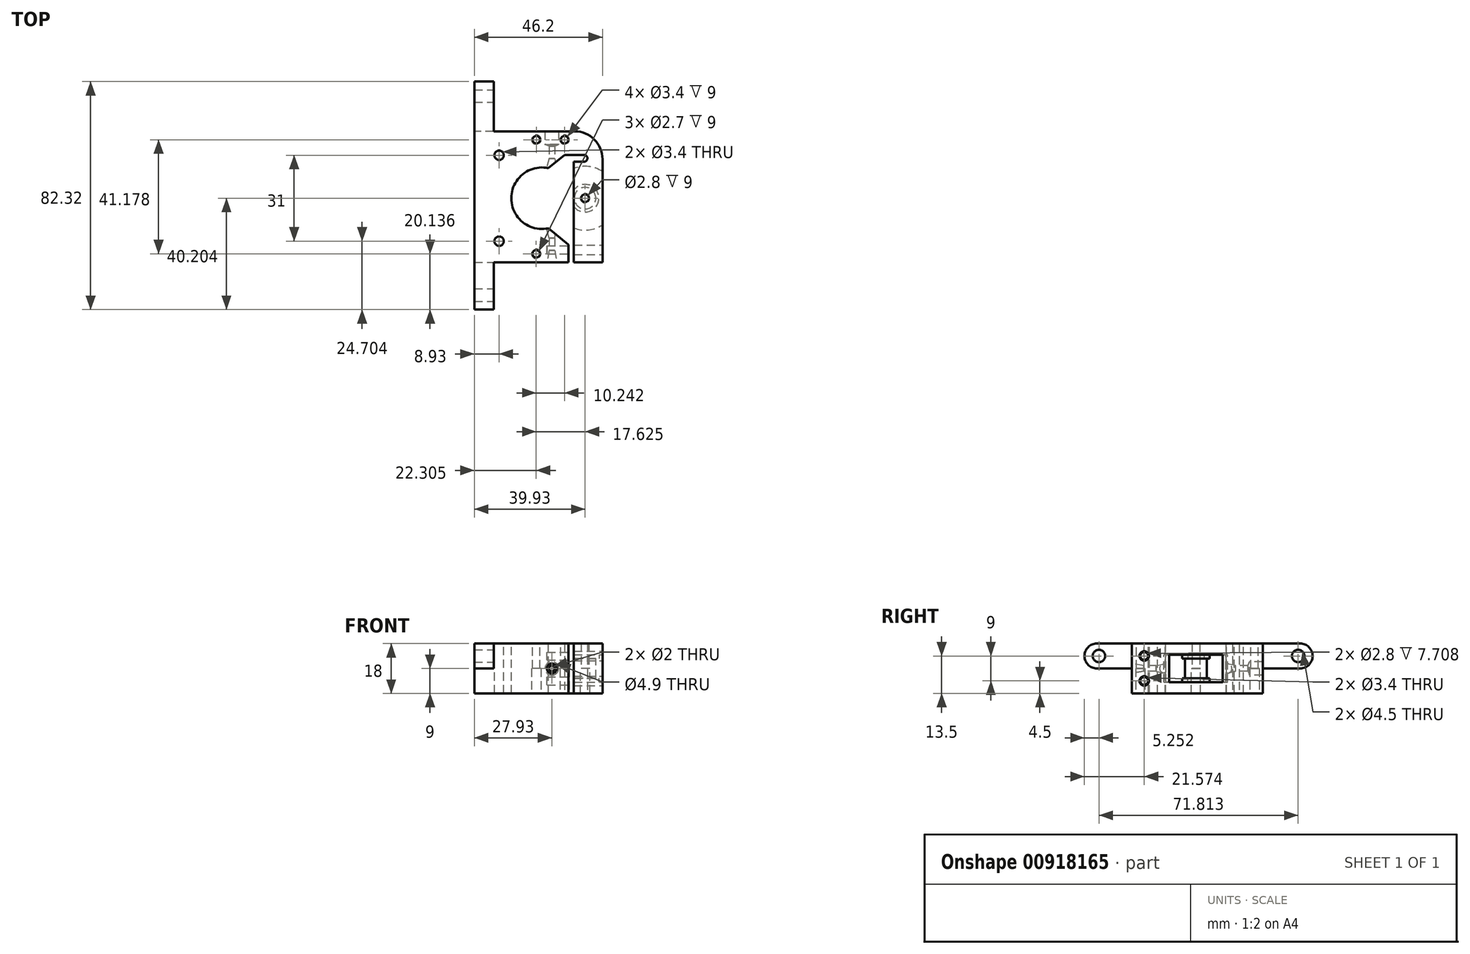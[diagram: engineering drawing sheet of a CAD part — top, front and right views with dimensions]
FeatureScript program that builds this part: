
annotation { "Feature Type Name" : "Feature", "Feature Type Description" : "" }
export const myFeature = defineFeature(function(context is Context, id is Id, definition is map)
    precondition{}
    {
        {
            var Q0;
            Q0=qCreatedBy(makeId("Top.planeOp"),FACE);
            var sketch = newSketch(context, id + "F0", { "sketchPlane" : qUnion([Q0])});
            skLineSegment(sketch, "E0", {"start": v(-24.43, 29.94) * mm, "end": v(-24.43, -17.36) * mm});
            skLineSegment(sketch, "E1", {"start": v(-24.43, -17.36) * mm, "end": v(-24.43, -17.36) * mm});
            skLineSegment(sketch, "E2", {"start": v(-24.43, -17.36) * mm, "end": v(-24.43, -17.35) * mm});
            skLineSegment(sketch, "E3", {"start": v(-24.43, -17.35) * mm, "end": v(9.48, -17.35) * mm});
            skLineSegment(sketch, "E4", {"start": v(9.48, -17.35) * mm, "end": v(9.48, 21.46) * mm});
            skLineSegment(sketch, "E5", {"start": v(9.48, 21.46) * mm, "end": v(15.14, 21.46) * mm});
            skLineSegment(sketch, "E6", {"start": v(15.14, 19) * mm, "end": v(11.48, 19) * mm});
            skLineSegment(sketch, "E7", {"start": v(11.48, 19) * mm, "end": v(11.48, -17.35) * mm});
            skLineSegment(sketch, "E8", {"start": v(11.48, -17.35) * mm, "end": v(21.77, -17.35) * mm});
            skLineSegment(sketch, "E9", {"start": v(21.77, -17.35) * mm, "end": v(21.77, 29.94) * mm});
            skLineSegment(sketch, "E10", {"start": v(21.77, 29.94) * mm, "end": v(-24.43, 29.94) * mm});
            skCircle(sketch, "E11", {"center": v(-2.07, 26.93) * mm, "radius": 1.35 * mm});
            skCircle(sketch, "E12", {"center": v(8.12, 26.93) * mm, "radius": 1.35 * mm});
            skCircle(sketch, "E13", {"center": v(-2.12, -14.24) * mm, "radius": 1.35 * mm});
            skArc(sketch, "E14", {"start": v(15.14, 19) * mm, "mid": v(16.36, 20.23) * mm, "end": v(15.14, 21.46) * mm});
            skCircle(sketch, "E15", {"center": v(-2.07, 26.93) * mm, "radius": 1.7 * mm});
            skCircle(sketch, "E16", {"center": v(8.12, 26.93) * mm, "radius": 1.7 * mm});
            skCircle(sketch, "E17", {"center": v(-2.12, -14.24) * mm, "radius": 1.7 * mm});
            skSolve(sketch);
        }
        {
            var Q0;
            Q0=makeQuery(id+"F0.imprint","IMPRINT",FACE,{"disambiguationData":[TD([[makeQuery(id+"F0.imprint","IMPRINT",EDGE,{"derivedFrom":sQuery(id+"F0.wireOp",EDGE,"E0")}),1.0]])]});
            extrude(context, id + "F1", {"entities" : qUnion([Q0]), "depth" : 9 * mm});
        }
        {
            var Q0;
            Q0=makeQuery(id+"F1.opExtrude","CAP_FACE",FACE,{"disambiguationData":[OSD([sQuery(id+"F0.wireOp",EDGE,"E0"),sQuery(id+"F0.wireOp",EDGE,"E1"),sQuery(id+"F0.wireOp",EDGE,"E2"),sQuery(id+"F0.wireOp",EDGE,"E3"),sQuery(id+"F0.wireOp",EDGE,"E4"),sQuery(id+"F0.wireOp",EDGE,"E5"),sQuery(id+"F0.wireOp",EDGE,"E6"),sQuery(id+"F0.wireOp",EDGE,"E7"),sQuery(id+"F0.wireOp",EDGE,"E8"),sQuery(id+"F0.wireOp",EDGE,"E9"),sQuery(id+"F0.wireOp",EDGE,"E10"),sQuery(id+"F0.wireOp",EDGE,"604cad85-587a-4b7d-8070-06f4cba85480"),sQuery(id+"F0.wireOp",EDGE,"6e5e38c1-5bff-4efe-a8c5-b84022f0a049"),sQuery(id+"F0.wireOp",EDGE,"b8144507-9dd7-4af4-87a3-7b649dd00ae6"),sQuery(id+"F0.wireOp",EDGE,"b9c2cb7c-5e58-4995-888e-a78f0403fbb5"),sQuery(id+"F0.wireOp",EDGE,"885990ab-7576-4c23-8475-595d2769e284"),sQuery(id+"F0.wireOp",EDGE,"E11"),sQuery(id+"F0.wireOp",EDGE,"E12"),sQuery(id+"F0.wireOp",EDGE,"E13"),sQuery(id+"F0.wireOp",EDGE,"E14")])],"isStart":false});
            var sketch = newSketch(context, id + "F2", { "sketchPlane" : qUnion([Q0])});
            skCircle(sketch, "E18", {"center": v(0, 5.82) * mm, "radius": 11.1 * mm});
            skCircle(sketch, "E19", {"center": v(-15.5, 21.32) * mm, "radius": 1.7 * mm});
            skCircle(sketch, "E20", {"center": v(-15.5, -9.68) * mm, "radius": 1.7 * mm});
            skSolve(sketch);
        }
        {
            var Q0;
            Q0=qSketchRegion(id+"F2",true);
            extrude(context, id + "F3", {"entities" : qUnion([Q0]), "operationType" : NewBodyOperationType.REMOVE, "endBound" : BoundingType.THROUGH_ALL, "oppositeDirection" : true, "depth" : 25 * mm});
        }
        {
            var Q0;
            Q0=makeQuery(id+"F1.opExtrude","CAP_FACE",FACE,{"disambiguationData":[OSD([sQuery(id+"F0.wireOp",EDGE,"E0"),sQuery(id+"F0.wireOp",EDGE,"E1"),sQuery(id+"F0.wireOp",EDGE,"E2"),sQuery(id+"F0.wireOp",EDGE,"E3"),sQuery(id+"F0.wireOp",EDGE,"E4"),sQuery(id+"F0.wireOp",EDGE,"E5"),sQuery(id+"F0.wireOp",EDGE,"E6"),sQuery(id+"F0.wireOp",EDGE,"E7"),sQuery(id+"F0.wireOp",EDGE,"E8"),sQuery(id+"F0.wireOp",EDGE,"E9"),sQuery(id+"F0.wireOp",EDGE,"E10"),sQuery(id+"F0.wireOp",EDGE,"604cad85-587a-4b7d-8070-06f4cba85480"),sQuery(id+"F0.wireOp",EDGE,"6e5e38c1-5bff-4efe-a8c5-b84022f0a049"),sQuery(id+"F0.wireOp",EDGE,"E11"),sQuery(id+"F0.wireOp",EDGE,"E12"),sQuery(id+"F0.wireOp",EDGE,"E13"),sQuery(id+"F0.wireOp",EDGE,"E14")])],"isStart":false});
            var sketch = newSketch(context, id + "F4", { "sketchPlane" : qUnion([Q0])});
            skCircle(sketch, "E21", {"center": v(15.5, 5.82) * mm, "radius": 11.5 * mm});
            skCircle(sketch, "E22", {"center": v(15.5, 5.82) * mm, "radius": 5 * mm});
            skCircle(sketch, "E23", {"center": v(15.5, 5.82) * mm, "radius": 3.9 * mm});
            skLineSegment(sketch, "E24", {"start": v(0, 5.82) * mm, "end": v(31, 5.82) * mm, "construction": true});
            skCircle(sketch, "E25", {"center": v(15.5, 5.82) * mm, "radius": 1.4 * mm});
            skCircle(sketch, "E26", {"center": v(15.5, 5.82) * mm, "radius": 1.7 * mm});
            skSolve(sketch);
        }
        {
            var Q0;
            Q0=makeQuery(id+"F4.imprint","IMPRINT",FACE,{"disambiguationData":[TD([[makeQuery(id+"F4.imprint","IMPRINT",EDGE,{"derivedFrom":sQuery(id+"F4.wireOp",EDGE,"E22")}),-1.0]])]});
            extrude(context, id + "F5", {"entities" : qUnion([Q0]), "operationType" : NewBodyOperationType.REMOVE, "oppositeDirection" : true, "depth" : 5 * mm});
        }
        {
            var Q0;
            Q0=makeQuery(id+"F4.imprint","IMPRINT",FACE,{"disambiguationData":[TD([[makeQuery(id+"F4.imprint","IMPRINT",EDGE,{"derivedFrom":sQuery(id+"F4.wireOp",EDGE,"E22")}),1.0]])]});
            var Q1;
            Q1=makeQuery(id+"F4.imprint","IMPRINT",FACE,{"disambiguationData":[TD([[makeQuery(id+"F4.imprint","IMPRINT",EDGE,{"derivedFrom":sQuery(id+"F4.wireOp",EDGE,"E23")}),-1.0]])]});
            extrude(context, id + "F6", {"entities" : qUnion([Q0, Q1]), "operationType" : NewBodyOperationType.REMOVE, "oppositeDirection" : true, "depth" : 3.5 * mm});
        }
        {
            var Q0;
            {var subQ0=sQuery(id+"F0.wireOp",EDGE,"E0");var subQ1=sQuery(id+"F0.wireOp",EDGE,"E1");var subQ2=sQuery(id+"F0.wireOp",EDGE,"E2");var subQ3=sQuery(id+"F0.wireOp",EDGE,"E3");var subQ4=sQuery(id+"F0.wireOp",EDGE,"E4");var subQ5=sQuery(id+"F0.wireOp",EDGE,"E5");var subQ6=sQuery(id+"F0.wireOp",EDGE,"E6");var subQ7=sQuery(id+"F0.wireOp",EDGE,"E7");var subQ8=sQuery(id+"F0.wireOp",EDGE,"E9");var subQ9=sQuery(id+"F0.wireOp",EDGE,"E10");var subQ10=sQuery(id+"F0.wireOp",EDGE,"604cad85-587a-4b7d-8070-06f4cba85480");var subQ11=sQuery(id+"F0.wireOp",EDGE,"6e5e38c1-5bff-4efe-a8c5-b84022f0a049");var subQ12=sQuery(id+"F0.wireOp",EDGE,"E11");var subQ13=sQuery(id+"F0.wireOp",EDGE,"E12");var subQ14=sQuery(id+"F0.wireOp",EDGE,"E13");var subQ15=sQuery(id+"F0.wireOp",EDGE,"E14");Q0=makeQuery(id+"F5.boolean.opBoolean","SPLIT",FACE,{"disambiguationData":[TD([makeQuery(id+"F1.opExtrude","SWEPT_FACE",FACE,{"disambiguationData":[OSD([subQ0])]})])],"derivedFrom":makeQuery(id+"F1.opExtrude","CAP_FACE",FACE,{"disambiguationData":[OSD([subQ0,subQ1,subQ2,subQ3,subQ4,subQ5,subQ6,subQ7,sQuery(id+"F0.wireOp",EDGE,"E8"),subQ8,subQ9,subQ10,subQ11,subQ12,subQ13,subQ14,subQ15])],"isStart":false})});}
            var sketch = newSketch(context, id + "F7", { "sketchPlane" : qUnion([Q0])});
            skLineSegment(sketch, "E27", {"start": v(2.5, 24.65) * mm, "end": v(2.5, 20.21) * mm});
            skLineSegment(sketch, "E28", {"start": v(2.5, 20.21) * mm, "end": v(1.31, 15.18) * mm});
            skLineSegment(sketch, "E29", {"start": v(1.31, 15.18) * mm, "end": v(3.5, 15.18) * mm});
            skLineSegment(sketch, "E30", {"start": v(3.5, 15.18) * mm, "end": v(3.5, 30.2) * mm});
            skLineSegment(sketch, "E31", {"start": v(0, 5.82) * mm, "end": v(31.4, 5.82) * mm, "construction": true});
            skLineSegment(sketch, "E32.1.MirrorCS", {"start": v(3.5, -3.53) * mm, "end": v(3.5, -18.54) * mm});
            skLineSegment(sketch, "E32.3.MirrorCS", {"start": v(1.31, -3.53) * mm, "end": v(3.5, -3.53) * mm});
            skLineSegment(sketch, "E32.4.MirrorCS", {"start": v(2.5, -8.56) * mm, "end": v(1.31, -3.53) * mm});
            skLineSegment(sketch, "E32.5.MirrorCS", {"start": v(2.5, -13) * mm, "end": v(2.5, -8.56) * mm});
            skLineSegment(sketch, "E32.6.MirrorCS", {"start": v(3.5, -18.54) * mm, "end": v(1.5, -18.54) * mm});
            skLineSegment(sketch, "E33", {"start": v(3.5, 30.2) * mm, "end": v(1.05, 30.2) * mm});
            skLineSegment(sketch, "E34", {"start": v(1.05, 30.2) * mm, "end": v(1.05, 25.2) * mm});
            skLineSegment(sketch, "E35", {"start": v(2.5, 24.65) * mm, "end": v(1.05, 25.2) * mm});
            skLineSegment(sketch, "E36", {"start": v(2.5, -13) * mm, "end": v(1.5, -18.54) * mm});
            skSolve(sketch);
        }
        {
            var Q0;
            Q0=qSketchRegion(id+"F7",true);
            var Q1;
            Q1=sQuery(id+"F7.wireOp",EDGE,"E30");
            revolve(context, id + "F8", {"entities" : qUnion([Q0]), "axis" : qUnion([Q1]), "revolveType" : RevolveType.FULL});
        }
        {
            var Q0;
            Q0=makeQuery(id+"F8.opRevolve","SWEPT_BODY",BODY,{"disambiguationData":[OSD([sQuery(id+"F7.wireOp",EDGE,"0e4a01cc-4869-4b9d-8ca2-1c94110d196d"),sQuery(id+"F7.wireOp",EDGE,"4d913e13-2244-4a79-84d2-82f6c5de00b3"),sQuery(id+"F7.wireOp",EDGE,"E27"),sQuery(id+"F7.wireOp",EDGE,"E28"),sQuery(id+"F7.wireOp",EDGE,"E29"),sQuery(id+"F7.wireOp",EDGE,"E30"),sQuery(id+"F7.wireOp",EDGE,"0bbee7b9-97e0-41c3-ac0e-625151f8027d")])]});
            var Q1;
            Q1=makeQuery(id+"F1.opExtrude","SWEPT_BODY",BODY,{"disambiguationData":[OSD([sQuery(id+"F0.wireOp",EDGE,"E0"),sQuery(id+"F0.wireOp",EDGE,"E1"),sQuery(id+"F0.wireOp",EDGE,"E2"),sQuery(id+"F0.wireOp",EDGE,"E3"),sQuery(id+"F0.wireOp",EDGE,"E4"),sQuery(id+"F0.wireOp",EDGE,"E5"),sQuery(id+"F0.wireOp",EDGE,"E6"),sQuery(id+"F0.wireOp",EDGE,"E7"),sQuery(id+"F0.wireOp",EDGE,"E8"),sQuery(id+"F0.wireOp",EDGE,"E9"),sQuery(id+"F0.wireOp",EDGE,"E10"),sQuery(id+"F0.wireOp",EDGE,"604cad85-587a-4b7d-8070-06f4cba85480"),sQuery(id+"F0.wireOp",EDGE,"6e5e38c1-5bff-4efe-a8c5-b84022f0a049"),sQuery(id+"F0.wireOp",EDGE,"E11"),sQuery(id+"F0.wireOp",EDGE,"E12"),sQuery(id+"F0.wireOp",EDGE,"E13"),sQuery(id+"F0.wireOp",EDGE,"E14")])]});
            booleanBodies(context, id + "F9", {"operationType" : BooleanOperationType.SUBTRACTION, "tools" : qUnion([Q0]), "targets" : qUnion([Q1]), "keepTools" : true});
        }
        {
            var Q0;
            Q0=makeQuery(id+"F8.opRevolve","SWEPT_BODY",BODY,{"disambiguationData":[OSD([sQuery(id+"F7.wireOp",EDGE,"E32.0.MirrorCS"),sQuery(id+"F7.wireOp",EDGE,"E32.1.MirrorCS"),sQuery(id+"F7.wireOp",EDGE,"E32.2.MirrorCS"),sQuery(id+"F7.wireOp",EDGE,"E32.3.MirrorCS"),sQuery(id+"F7.wireOp",EDGE,"E32.4.MirrorCS"),sQuery(id+"F7.wireOp",EDGE,"E32.5.MirrorCS"),sQuery(id+"F7.wireOp",EDGE,"E32.6.MirrorCS")])]});
            var Q1;
            Q1=makeQuery(id+"F1.opExtrude","SWEPT_BODY",BODY,{"disambiguationData":[OSD([sQuery(id+"F0.wireOp",EDGE,"E0"),sQuery(id+"F0.wireOp",EDGE,"E1"),sQuery(id+"F0.wireOp",EDGE,"E2"),sQuery(id+"F0.wireOp",EDGE,"E3"),sQuery(id+"F0.wireOp",EDGE,"E4"),sQuery(id+"F0.wireOp",EDGE,"E5"),sQuery(id+"F0.wireOp",EDGE,"E6"),sQuery(id+"F0.wireOp",EDGE,"E7"),sQuery(id+"F0.wireOp",EDGE,"E8"),sQuery(id+"F0.wireOp",EDGE,"E9"),sQuery(id+"F0.wireOp",EDGE,"E10"),sQuery(id+"F0.wireOp",EDGE,"604cad85-587a-4b7d-8070-06f4cba85480"),sQuery(id+"F0.wireOp",EDGE,"6e5e38c1-5bff-4efe-a8c5-b84022f0a049"),sQuery(id+"F0.wireOp",EDGE,"E11"),sQuery(id+"F0.wireOp",EDGE,"E12"),sQuery(id+"F0.wireOp",EDGE,"E13"),sQuery(id+"F0.wireOp",EDGE,"E14")])]});
            booleanBodies(context, id + "F10", {"operationType" : BooleanOperationType.SUBTRACTION, "tools" : qUnion([Q0]), "targets" : qUnion([Q1]), "keepTools" : true});
        }
        {
            var Q0;
            Q0=makeQuery(id+"F1.opExtrude","SWEPT_EDGE",EDGE,{"disambiguationData":[OSD([sQuery(id+"F0.wireOp",EDGE,"E9"),sQuery(id+"F0.wireOp",EDGE,"E10")])]});
            fillet(context, id + "F11", {"entities" : qUnion([Q0]), "radius" : 10 * mm, "tangentPropagation" : true, "allowEdgeOverflow" : false});
        }
        {
            var Q0;
            Q0=qSketchRegion(id+"F0",true);
            var Q1;
            Q1=makeQuery(id+"F0.imprint","IMPRINT",FACE,{"disambiguationData":[TD([[makeQuery(id+"F0.imprint","IMPRINT",EDGE,{"derivedFrom":sQuery(id+"F0.wireOp",EDGE,"E12")}),-1.0]])]});
            var Q2;
            Q2=makeQuery(id+"F0.imprint","IMPRINT",FACE,{"disambiguationData":[TD([[makeQuery(id+"F0.imprint","IMPRINT",EDGE,{"derivedFrom":sQuery(id+"F0.wireOp",EDGE,"E11")}),-1.0]])]});
            var Q3;
            Q3=makeQuery(id+"F0.imprint","IMPRINT",FACE,{"disambiguationData":[TD([[makeQuery(id+"F0.imprint","IMPRINT",EDGE,{"derivedFrom":sQuery(id+"F0.wireOp",EDGE,"E13")}),-1.0]])]});
            extrude(context, id + "F12", {"entities" : qUnion([Q0, Q1, Q2, Q3]), "oppositeDirection" : true, "depth" : 9 * mm});
        }
        {
            var Q0;
            Q0=makeQuery(id+"F12.opExtrude","SWEPT_BODY",BODY,{"disambiguationData":[OSD([sQuery(id+"F0.wireOp",EDGE,"E0"),sQuery(id+"F0.wireOp",EDGE,"E3"),sQuery(id+"F0.wireOp",EDGE,"E4"),sQuery(id+"F0.wireOp",EDGE,"E5"),sQuery(id+"F0.wireOp",EDGE,"E6"),sQuery(id+"F0.wireOp",EDGE,"E7"),sQuery(id+"F0.wireOp",EDGE,"E8"),sQuery(id+"F0.wireOp",EDGE,"E9"),sQuery(id+"F0.wireOp",EDGE,"E10"),sQuery(id+"F0.wireOp",EDGE,"E11"),sQuery(id+"F0.wireOp",EDGE,"E12"),sQuery(id+"F0.wireOp",EDGE,"E13"),sQuery(id+"F0.wireOp",EDGE,"E14")])]});
            transform(context, id + "F13", {"entities" : qUnion([Q0]), "transformType" : TransformType.TRANSLATION_3D, "dx" : 0 * mm, "dy" : 0 * mm, "dz" : 18 * mm, "makeCopy" : false});
        }
        {
            var Q0;
            Q0=makeQuery(id+"F12.opExtrude","SWEPT_EDGE",EDGE,{"disambiguationData":[OSD([sQuery(id+"F0.wireOp",EDGE,"E9"),sQuery(id+"F0.wireOp",EDGE,"E10")])]});
            fillet(context, id + "F14", {"entities" : qUnion([Q0]), "radius" : 10 * mm, "tangentPropagation" : true, "allowEdgeOverflow" : false});
        }
        {
            var Q0;
            Q0=qSketchRegion(id+"F2",true);
            extrude(context, id + "F15", {"entities" : qUnion([Q0]), "operationType" : NewBodyOperationType.REMOVE, "endBound" : BoundingType.THROUGH_ALL, "depth" : 25 * mm});
        }
        {
            var Q0;
            {var subQ3=sQuery(id+"F4.wireOp",EDGE,"E21");var subQ7=makeQuery(id+"F1.opExtrude","CAP_EDGE",EDGE,{"disambiguationData":[OSD([sQuery(id+"F0.wireOp",EDGE,"E9")])],"isStart":false});var subQ9=makeQuery(id+"F4.imprint","INTERSECT",VERTEX,{"disambiguationData":[OD(0.0)],"derivedFrom":[subQ7,subQ3]});Q0=makeQuery(id+"F4.imprint","IMPRINT",FACE,{"disambiguationData":[TD([[makeQuery(id+"F4.imprint","IMPRINT",EDGE,{"disambiguationData":[TD([[subQ9,-1.0]])],"derivedFrom":subQ3}),1.0]])]});}
            extrude(context, id + "F16", {"entities" : qUnion([Q0]), "operationType" : NewBodyOperationType.REMOVE, "depth" : 5 * mm});
        }
        {
            var Q0;
            Q0=makeQuery(id+"F4.imprint","IMPRINT",FACE,{"disambiguationData":[TD([[makeQuery(id+"F4.imprint","IMPRINT",EDGE,{"derivedFrom":sQuery(id+"F4.wireOp",EDGE,"E23")}),-1.0]])]});
            extrude(context, id + "F17", {"entities" : qUnion([Q0]), "operationType" : NewBodyOperationType.REMOVE, "depth" : 3.5 * mm});
        }
        {
            var Q0;
            Q0=makeQuery(id+"F8.opRevolve","SWEPT_BODY",BODY,{"disambiguationData":[OSD([sQuery(id+"F7.wireOp",EDGE,"0e4a01cc-4869-4b9d-8ca2-1c94110d196d"),sQuery(id+"F7.wireOp",EDGE,"4d913e13-2244-4a79-84d2-82f6c5de00b3"),sQuery(id+"F7.wireOp",EDGE,"E27"),sQuery(id+"F7.wireOp",EDGE,"E28"),sQuery(id+"F7.wireOp",EDGE,"E29"),sQuery(id+"F7.wireOp",EDGE,"E30"),sQuery(id+"F7.wireOp",EDGE,"0bbee7b9-97e0-41c3-ac0e-625151f8027d")])]});
            var Q1;
            Q1=makeQuery(id+"F12.opExtrude","SWEPT_BODY",BODY,{"disambiguationData":[OSD([sQuery(id+"F0.wireOp",EDGE,"E0"),sQuery(id+"F0.wireOp",EDGE,"E3"),sQuery(id+"F0.wireOp",EDGE,"E4"),sQuery(id+"F0.wireOp",EDGE,"E5"),sQuery(id+"F0.wireOp",EDGE,"E6"),sQuery(id+"F0.wireOp",EDGE,"E7"),sQuery(id+"F0.wireOp",EDGE,"E8"),sQuery(id+"F0.wireOp",EDGE,"E9"),sQuery(id+"F0.wireOp",EDGE,"E10"),sQuery(id+"F0.wireOp",EDGE,"E11"),sQuery(id+"F0.wireOp",EDGE,"E12"),sQuery(id+"F0.wireOp",EDGE,"E13"),sQuery(id+"F0.wireOp",EDGE,"E14")])]});
            booleanBodies(context, id + "F18", {"operationType" : BooleanOperationType.SUBTRACTION, "tools" : qUnion([Q0]), "targets" : qUnion([Q1])});
        }
        {
            var Q0;
            Q0=makeQuery(id+"F8.opRevolve","SWEPT_BODY",BODY,{"disambiguationData":[OSD([sQuery(id+"F7.wireOp",EDGE,"E32.0.MirrorCS"),sQuery(id+"F7.wireOp",EDGE,"E32.1.MirrorCS"),sQuery(id+"F7.wireOp",EDGE,"E32.2.MirrorCS"),sQuery(id+"F7.wireOp",EDGE,"E32.3.MirrorCS"),sQuery(id+"F7.wireOp",EDGE,"E32.4.MirrorCS"),sQuery(id+"F7.wireOp",EDGE,"E32.5.MirrorCS"),sQuery(id+"F7.wireOp",EDGE,"E32.6.MirrorCS")])]});
            var Q1;
            Q1=makeQuery(id+"F12.opExtrude","SWEPT_BODY",BODY,{"disambiguationData":[OSD([sQuery(id+"F0.wireOp",EDGE,"E0"),sQuery(id+"F0.wireOp",EDGE,"E3"),sQuery(id+"F0.wireOp",EDGE,"E4"),sQuery(id+"F0.wireOp",EDGE,"E5"),sQuery(id+"F0.wireOp",EDGE,"E6"),sQuery(id+"F0.wireOp",EDGE,"E7"),sQuery(id+"F0.wireOp",EDGE,"E8"),sQuery(id+"F0.wireOp",EDGE,"E9"),sQuery(id+"F0.wireOp",EDGE,"E10"),sQuery(id+"F0.wireOp",EDGE,"E11"),sQuery(id+"F0.wireOp",EDGE,"E12"),sQuery(id+"F0.wireOp",EDGE,"E13"),sQuery(id+"F0.wireOp",EDGE,"E14")])]});
            booleanBodies(context, id + "F19", {"operationType" : BooleanOperationType.SUBTRACTION, "tools" : qUnion([Q0]), "targets" : qUnion([Q1])});
        }
        {
            var Q0;
            Q0=makeQuery(id+"F12.opExtrude","SWEPT_FACE",FACE,{"disambiguationData":[OSD([sQuery(id+"F0.wireOp",EDGE,"E9")])]});
            var sketch = newSketch(context, id + "F20", { "sketchPlane" : qUnion([Q0])});
            skCircle(sketch, "E37", {"center": v(-12.8, 13.5) * mm, "radius": 1.7 * mm});
            skCircle(sketch, "E38", {"center": v(-12.8, 13.5) * mm, "radius": 1.4 * mm});
            skCircle(sketch, "E39", {"center": v(-12.8, 4.5) * mm, "radius": 1.7 * mm});
            skCircle(sketch, "E40", {"center": v(-12.8, 4.5) * mm, "radius": 1.4 * mm});
            skSolve(sketch);
        }
        {
            var Q0;
            Q0=makeQuery(id+"F20.imprint","IMPRINT",FACE,{"disambiguationData":[TD([[makeQuery(id+"F20.imprint","IMPRINT",EDGE,{"derivedFrom":sQuery(id+"F20.wireOp",EDGE,"E38")}),1.0]])]});
            extrude(context, id + "F21", {"entities" : qUnion([Q0]), "operationType" : NewBodyOperationType.REMOVE, "oppositeDirection" : true, "depth" : 20 * mm});
        }
        {
            var Q0;
            Q0=makeQuery(id+"F20.imprint","IMPRINT",FACE,{"disambiguationData":[TD([[makeQuery(id+"F20.imprint","IMPRINT",EDGE,{"derivedFrom":sQuery(id+"F20.wireOp",EDGE,"E37")}),1.0]])]});
            extrude(context, id + "F22", {"entities" : qUnion([Q0]), "operationType" : NewBodyOperationType.REMOVE, "oppositeDirection" : true, "depth" : 11 * mm});
        }
        {
            var Q0;
            Q0=makeQuery(id+"F20.imprint","IMPRINT",FACE,{"disambiguationData":[TD([[makeQuery(id+"F20.imprint","IMPRINT",EDGE,{"derivedFrom":sQuery(id+"F20.wireOp",EDGE,"E40")}),1.0]])]});
            extrude(context, id + "F23", {"entities" : qUnion([Q0]), "operationType" : NewBodyOperationType.REMOVE, "oppositeDirection" : true, "depth" : 20 * mm});
        }
        {
            var Q0;
            Q0=makeQuery(id+"F20.imprint","IMPRINT",FACE,{"disambiguationData":[TD([[makeQuery(id+"F20.imprint","IMPRINT",EDGE,{"derivedFrom":sQuery(id+"F20.wireOp",EDGE,"E39")}),1.0]])]});
            extrude(context, id + "F24", {"entities" : qUnion([Q0]), "operationType" : NewBodyOperationType.REMOVE, "oppositeDirection" : true, "depth" : 11 * mm});
        }
        {
            var Q0;
            Q0=makeQuery(id+"F4.imprint","IMPRINT",FACE,{"disambiguationData":[TD([[makeQuery(id+"F4.imprint","IMPRINT",EDGE,{"derivedFrom":sQuery(id+"F4.wireOp",EDGE,"E25")}),1.0]])]});
            var Q1;
            Q1=makeQuery(id+"F4.imprint","IMPRINT",FACE,{"disambiguationData":[TD([[makeQuery(id+"F4.imprint","IMPRINT",EDGE,{"derivedFrom":sQuery(id+"F4.wireOp",EDGE,"E25")}),-1.0]])]});
            extrude(context, id + "F25", {"entities" : qUnion([Q0, Q1]), "operationType" : NewBodyOperationType.REMOVE, "oppositeDirection" : true, "depth" : 25 * mm});
        }
        {
            var Q0;
            Q0=makeQuery(id+"F4.imprint","IMPRINT",FACE,{"disambiguationData":[TD([[makeQuery(id+"F4.imprint","IMPRINT",EDGE,{"derivedFrom":sQuery(id+"F4.wireOp",EDGE,"E25")}),1.0]])]});
            extrude(context, id + "F26", {"entities" : qUnion([Q0]), "operationType" : NewBodyOperationType.REMOVE, "depth" : 25 * mm});
        }
        {
            var Q0;
            Q0=makeQuery(id+"F12.opExtrude","SWEPT_FACE",FACE,{"disambiguationData":[OSD([sQuery(id+"F0.wireOp",EDGE,"E10")])]});
            var sketch = newSketch(context, id + "F27", { "sketchPlane" : qUnion([Q0])});
            skLineSegment(sketch, "E41.bottom", {"start": v(24.43, 9) * mm, "end": v(17.43, 9) * mm});
            skLineSegment(sketch, "E41.top", {"start": v(24.43, 18) * mm, "end": v(17.43, 18) * mm});
            skLineSegment(sketch, "E41.left", {"start": v(24.43, 9) * mm, "end": v(24.43, 18) * mm});
            skLineSegment(sketch, "E41.right", {"start": v(17.43, 9) * mm, "end": v(17.43, 18) * mm});
            skSolve(sketch);
        }
        {
            var Q0;
            Q0=qSketchRegion(id+"F27",true);
            extrude(context, id + "F28", {"entities" : qUnion([Q0]), "operationType" : NewBodyOperationType.ADD, "depth" : 18 * mm, "hasSecondDirection" : true, "secondDirectionOppositeDirection" : true, "secondDirectionDepth" : 64.31 * mm});
        }
        {
            var Q0;
            {var subQ0=sQuery(id+"F27.wireOp",EDGE,"E41.right");var subQ3=sQuery(id+"F0.wireOp",EDGE,"E3");Q0=makeQuery(id+"F28.boolean.opBoolean","SPLIT",FACE,{"disambiguationData":[TD([makeQuery(id+"F12.opExtrude","SWEPT_FACE",FACE,{"disambiguationData":[OSD([subQ3])]})])],"derivedFrom":makeQuery(id+"F28.opExtrude","SWEPT_FACE",FACE,{"disambiguationData":[OSD([subQ0])]})});}
            var sketch = newSketch(context, id + "F29", { "sketchPlane" : qUnion([Q0])});
            skCircle(sketch, "E42", {"center": v(-29.13, 13.5) * mm, "radius": 2.25 * mm});
            skPoint(sketch, "E43", {"position": v(-34.38, 13.5) * mm});
            skSolve(sketch);
        }
        {
            var Q0;
            {var subQ0=sQuery(id+"F27.wireOp",EDGE,"E41.right");var subQ3=sQuery(id+"F0.wireOp",EDGE,"E10");Q0=makeQuery(id+"F28.boolean.opBoolean","SPLIT",FACE,{"disambiguationData":[TD([makeQuery(id+"F12.opExtrude","SWEPT_FACE",FACE,{"disambiguationData":[OSD([subQ3])]})])],"derivedFrom":makeQuery(id+"F28.opExtrude","SWEPT_FACE",FACE,{"disambiguationData":[OSD([subQ0])]})});}
            var sketch = newSketch(context, id + "F30", { "sketchPlane" : qUnion([Q0])});
            skCircle(sketch, "E44", {"center": v(42.69, 13.5) * mm, "radius": 2.25 * mm});
            skPoint(sketch, "E45", {"position": v(47.94, 13.5) * mm});
            skSolve(sketch);
        }
        {
            var Q0;
            Q0=qSketchRegion(id+"F29",true);
            var Q1;
            Q1=qSketchRegion(id+"F30",true);
            extrude(context, id + "F31", {"entities" : qUnion([Q0, Q1]), "operationType" : NewBodyOperationType.REMOVE, "oppositeDirection" : true, "depth" : 25 * mm});
        }
        {
            var Q0;
            Q0=makeQuery(id+"F28.opExtrude","CAP_EDGE",EDGE,{"disambiguationData":[OSD([sQuery(id+"F27.wireOp",EDGE,"E41.top")])],"isStart":true});
            var Q1;
            Q1=makeQuery(id+"F28.opExtrude","CAP_EDGE",EDGE,{"disambiguationData":[OSD([sQuery(id+"F27.wireOp",EDGE,"E41.bottom")])],"isStart":true});
            var Q2;
            Q2=makeQuery(id+"F28.opExtrude","CAP_EDGE",EDGE,{"disambiguationData":[OSD([sQuery(id+"F27.wireOp",EDGE,"E41.top")])],"isStart":false});
            var Q3;
            Q3=makeQuery(id+"F28.opExtrude","CAP_EDGE",EDGE,{"disambiguationData":[OSD([sQuery(id+"F27.wireOp",EDGE,"E41.bottom")])],"isStart":false});
            fillet(context, id + "F32", {"entities" : qUnion([Q0, Q1, Q2, Q3]), "radius" : 4.5 * mm, "tangentPropagation" : true, "allowEdgeOverflow" : false});
        }
        {
            var Q0;
            Q0=makeQuery(id+"F3.boolean.opBoolean","INTERSECT",EDGE,{"disambiguationData":[OD(0.0)],"derivedFrom":[makeQuery(id+"F1.opExtrude","SWEPT_FACE",FACE,{"disambiguationData":[OSD([sQuery(id+"F0.wireOp",EDGE,"E4")])]}),makeQuery(id+"F3.opExtrude","SWEPT_FACE",FACE,{"disambiguationData":[OSD([sQuery(id+"F2.wireOp",EDGE,"E18")])]})]});
            var Q1;
            Q1=makeQuery(id+"F3.boolean.opBoolean","INTERSECT",EDGE,{"disambiguationData":[OD(1.0)],"derivedFrom":[makeQuery(id+"F1.opExtrude","SWEPT_FACE",FACE,{"disambiguationData":[OSD([sQuery(id+"F0.wireOp",EDGE,"E4")])]}),makeQuery(id+"F3.opExtrude","SWEPT_FACE",FACE,{"disambiguationData":[OSD([sQuery(id+"F2.wireOp",EDGE,"E18")])]})]});
            var Q2;
            Q2=makeQuery(id+"F15.boolean.opBoolean","INTERSECT",EDGE,{"disambiguationData":[OD(1.0)],"derivedFrom":[makeQuery(id+"F12.opExtrude","SWEPT_FACE",FACE,{"disambiguationData":[OSD([sQuery(id+"F0.wireOp",EDGE,"E4")])]}),makeQuery(id+"F15.opExtrude","SWEPT_FACE",FACE,{"disambiguationData":[OSD([sQuery(id+"F2.wireOp",EDGE,"E18")])]})]});
            var Q3;
            Q3=makeQuery(id+"F15.boolean.opBoolean","INTERSECT",EDGE,{"disambiguationData":[OD(0.0)],"derivedFrom":[makeQuery(id+"F12.opExtrude","SWEPT_FACE",FACE,{"disambiguationData":[OSD([sQuery(id+"F0.wireOp",EDGE,"E4")])]}),makeQuery(id+"F15.opExtrude","SWEPT_FACE",FACE,{"disambiguationData":[OSD([sQuery(id+"F2.wireOp",EDGE,"E18")])]})]});
            chamfer(context, id + "F33", {"entities" : qUnion([Q0, Q1, Q2, Q3]), "width" : 6 * mm, "tangentPropagation" : true});
        }
    });
